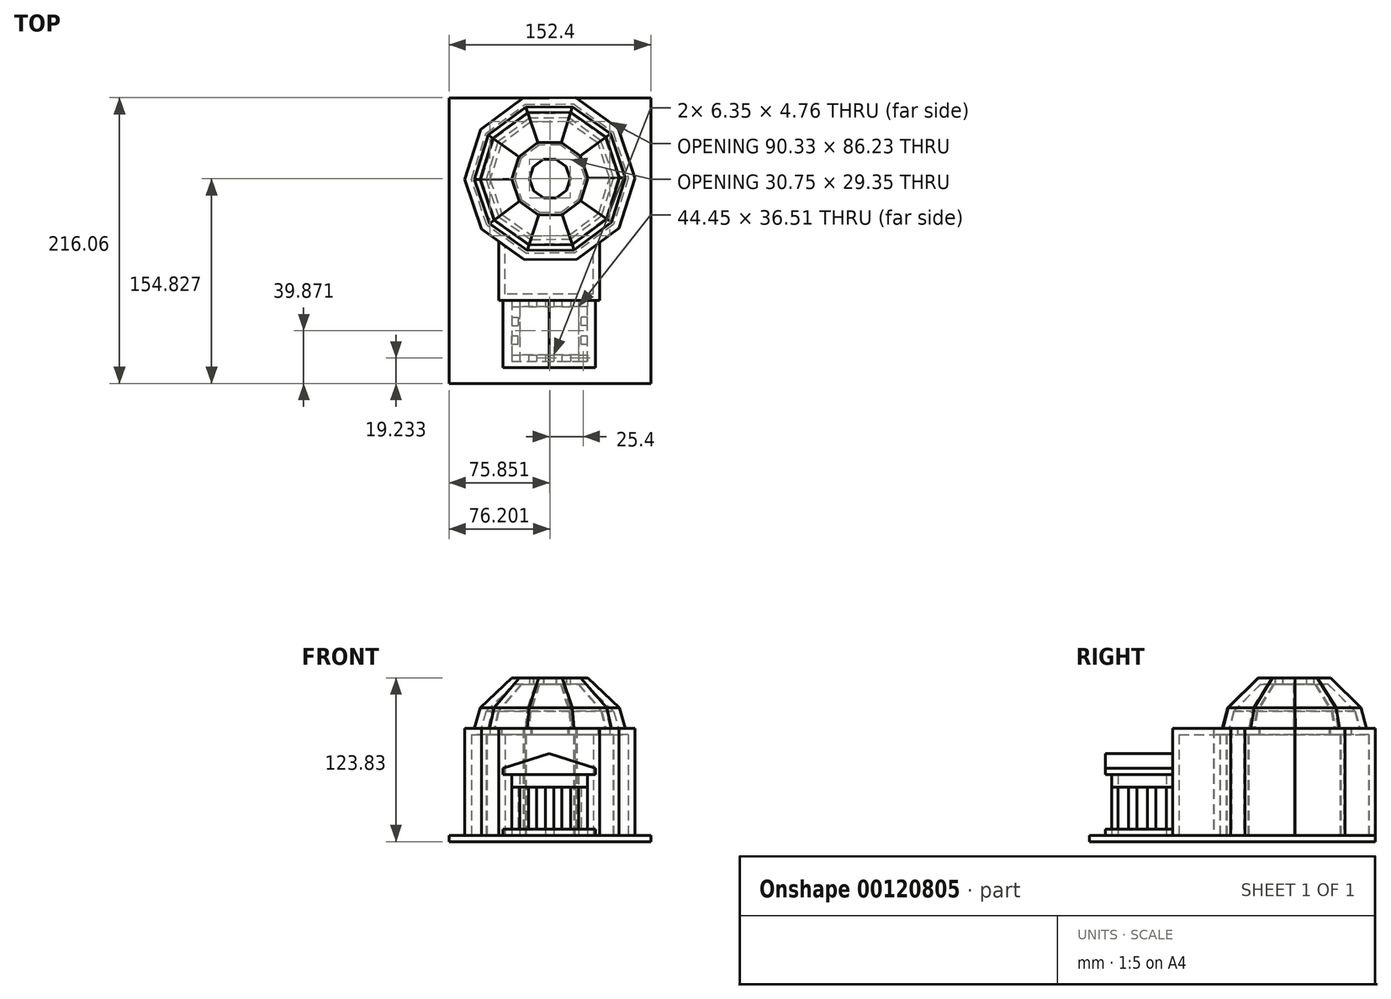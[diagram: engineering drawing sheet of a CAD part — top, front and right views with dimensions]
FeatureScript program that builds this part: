
annotation { "Feature Type Name" : "Feature", "Feature Type Description" : "" }
export const myFeature = defineFeature(function(context is Context, id is Id, definition is map)
    precondition{}
    {
        {
            var Q0;
            Q0=qCreatedBy(makeId("Top.planeOp"),FACE);
            var sketch = newSketch(context, id + "F0", { "sketchPlane" : qUnion([Q0])});
            skLineSegment(sketch, "E0.bottom", {"start": v(-75.7, 133.56) * mm, "end": v(76.7, 133.56) * mm});
            skLineSegment(sketch, "E0.top", {"start": v(-75.7, -82.34) * mm, "end": v(76.7, -82.34) * mm});
            skLineSegment(sketch, "E0.left", {"start": v(-75.7, 133.56) * mm, "end": v(-75.7, -82.34) * mm});
            skLineSegment(sketch, "E0.right", {"start": v(76.7, 133.56) * mm, "end": v(76.7, -82.34) * mm});
            skSolve(sketch);
        }
        {
            var Q0;
            Q0=qSketchRegion(id+"F0",true);
            var Q1;
            Q1=qSketchRegion(id+"FxzeoTgwMsGnq95_1",true);
            extrude(context, id + "F1", {"entities" : qUnion([Q0, Q1]), "depth" : 4.76 * mm});
        }
        {
            var Q0;
            Q0=makeQuery(id+"F1.opExtrude","CAP_FACE",FACE,{"disambiguationData":[OSD([sQuery(id+"F0.wireOp",EDGE,"E0.bottom"),sQuery(id+"F0.wireOp",EDGE,"E0.top"),sQuery(id+"F0.wireOp",EDGE,"E0.left"),sQuery(id+"F0.wireOp",EDGE,"E0.right")])],"isStart":false});
            var sketch = newSketch(context, id + "F2", { "sketchPlane" : qUnion([Q0])});
            skCircle(sketch, "E1.cCircle", {"center": v(0.5, 72.49) * mm, "radius": 61.07 * mm, "construction": true});
            skPoint(sketch, "E1.cCircle.centerSnap0", {"position": v(0.5, 133.56) * mm});
            skPoint(sketch, "E1.cCircle.perimeterSnap0", {"position": v(0.5, 133.56) * mm});
            skLineSegment(sketch, "E1.0", {"start": v(-19.84, 133.4) * mm, "end": v(19.84, 133.72) * mm});
            skLineSegment(sketch, "E1.1", {"start": v(19.84, 133.72) * mm, "end": v(52.14, 110.65) * mm});
            skLineSegment(sketch, "E1.2", {"start": v(52.14, 110.65) * mm, "end": v(64.7, 73) * mm});
            skLineSegment(sketch, "E1.3", {"start": v(64.7, 73) * mm, "end": v(52.74, 35.16) * mm});
            skLineSegment(sketch, "E1.4", {"start": v(52.74, 35.16) * mm, "end": v(20.82, 11.58) * mm});
            skLineSegment(sketch, "E1.5", {"start": v(20.82, 11.58) * mm, "end": v(-18.86, 11.26) * mm});
            skLineSegment(sketch, "E1.6", {"start": v(-18.86, 11.26) * mm, "end": v(-51.16, 34.33) * mm});
            skLineSegment(sketch, "E1.7", {"start": v(-51.16, 34.33) * mm, "end": v(-63.72, 71.97) * mm});
            skLineSegment(sketch, "E1.8", {"start": v(-63.72, 71.97) * mm, "end": v(-51.76, 109.81) * mm});
            skLineSegment(sketch, "E1.9", {"start": v(-51.76, 109.81) * mm, "end": v(-19.84, 133.4) * mm});
            skPoint(sketch, "E1.0.midPoint", {"position": v(0, 133.56) * mm});
            skPoint(sketch, "E1.0.midPoint.positionSnap0", {"position": v(0.5, 133.56) * mm});
            skCircle(sketch, "E2.cCircle", {"center": v(0.5, 72.49) * mm, "radius": 42.96 * mm, "construction": true});
            skLineSegment(sketch, "E2.0", {"start": v(-13.96, 115.28) * mm, "end": v(13.96, 115.6) * mm});
            skLineSegment(sketch, "E2.1", {"start": v(13.96, 115.6) * mm, "end": v(36.73, 99.45) * mm});
            skLineSegment(sketch, "E2.2", {"start": v(36.73, 99.45) * mm, "end": v(45.65, 73) * mm});
            skLineSegment(sketch, "E2.3", {"start": v(45.65, 73) * mm, "end": v(37.33, 46.36) * mm});
            skLineSegment(sketch, "E2.4", {"start": v(37.33, 46.36) * mm, "end": v(14.94, 29.7) * mm});
            skLineSegment(sketch, "E2.5", {"start": v(14.94, 29.7) * mm, "end": v(-12.97, 29.37) * mm});
            skLineSegment(sketch, "E2.6", {"start": v(-12.97, 29.37) * mm, "end": v(-35.74, 45.52) * mm});
            skLineSegment(sketch, "E2.7", {"start": v(-35.74, 45.52) * mm, "end": v(-44.67, 71.97) * mm});
            skLineSegment(sketch, "E2.8", {"start": v(-44.67, 71.97) * mm, "end": v(-36.35, 98.62) * mm});
            skLineSegment(sketch, "E2.9", {"start": v(-36.35, 98.62) * mm, "end": v(-13.96, 115.28) * mm});
            skPoint(sketch, "E2.0.midPoint", {"position": v(0, 115.44) * mm});
            skSolve(sketch);
        }
        {
            var Q0;
            Q0=qSketchRegion(id+"F2",true);
            var Q1;
            Q1=makeQuery(id+"F2.imprint","IMPRINT",FACE,{"disambiguationData":[TD([[makeQuery(id+"F2.imprint","IMPRINT",EDGE,{"derivedFrom":sQuery(id+"F2.wireOp",EDGE,"E2.0")}),-1.0]])]});
            extrude(context, id + "F3", {"entities" : qUnion([Q0, Q1]), "depth" : 80.96 * mm});
        }
        {
            var Q0;
            Q0=makeQuery(id+"F3.opExtrude","CAP_FACE",FACE,{"disambiguationData":[OSD([sQuery(id+"F2.wireOp",EDGE,"E1.0"),sQuery(id+"F2.wireOp",EDGE,"E1.1"),sQuery(id+"F2.wireOp",EDGE,"E1.2"),sQuery(id+"F2.wireOp",EDGE,"E1.3"),sQuery(id+"F2.wireOp",EDGE,"E1.4"),sQuery(id+"F2.wireOp",EDGE,"E1.5"),sQuery(id+"F2.wireOp",EDGE,"E1.6"),sQuery(id+"F2.wireOp",EDGE,"E1.7"),sQuery(id+"F2.wireOp",EDGE,"E1.8"),sQuery(id+"F2.wireOp",EDGE,"E1.9")])],"isStart":true});
            shell(context, id + "F4", {"entities" : qUnion([Q0]), "thickness" : 4.76 * mm});
        }
        {
            var Q0;
            Q0=makeQuery(id+"F2.imprint","IMPRINT",FACE,{"disambiguationData":[TD([[makeQuery(id+"F2.imprint","IMPRINT",EDGE,{"derivedFrom":sQuery(id+"F2.wireOp",EDGE,"E2.0")}),-1.0]])]});
            extrude(context, id + "F5", {"entities" : qUnion([Q0]), "operationType" : NewBodyOperationType.REMOVE, "endBound" : BoundingType.THROUGH_ALL, "depth" : 148.13 * mm});
        }
        {
            var Q0;
            Q0=makeQuery(id+"F1.opExtrude","CAP_FACE",FACE,{"disambiguationData":[OSD([sQuery(id+"F0.wireOp",EDGE,"E0.bottom"),sQuery(id+"F0.wireOp",EDGE,"E0.top"),sQuery(id+"F0.wireOp",EDGE,"E0.left"),sQuery(id+"F0.wireOp",EDGE,"E0.right")])],"isStart":false});
            var sketch = newSketch(context, id + "F6", { "sketchPlane" : qUnion([Q0])});
            skLineSegment(sketch, "E3.bottom", {"start": v(38.1, -19.45) * mm, "end": v(-38.1, -19.45) * mm});
            skLineSegment(sketch, "E3.top", {"start": v(38.1, 25) * mm, "end": v(-38.1, 25) * mm});
            skLineSegment(sketch, "E3.left", {"start": v(38.1, -19.45) * mm, "end": v(38.1, 25) * mm});
            skLineSegment(sketch, "E3.right", {"start": v(-38.1, -19.45) * mm, "end": v(-38.1, 25) * mm});
            skPoint(sketch, "E3.middle", {"position": v(0, 2.77) * mm});
            skLineSegment(sketch, "E4.0", {"start": v(-18.86, 11.26) * mm, "end": v(-51.16, 34.33) * mm});
            skLineSegment(sketch, "E5.0", {"start": v(20.82, 11.58) * mm, "end": v(-18.86, 11.26) * mm});
            skLineSegment(sketch, "E6.0", {"start": v(52.74, 35.16) * mm, "end": v(20.82, 11.58) * mm});
            skSolve(sketch);
        }
        {
            var Q0;
            {var subQ4=sQuery(id+"F6.wireOp",EDGE,"E3.bottom");Q0=makeQuery(id+"F6.imprint","IMPRINT",FACE,{"disambiguationData":[TD([[makeQuery(id+"F6.imprint","IMPRINT",EDGE,{"derivedFrom":subQ4}),-1.0]])]});}
            extrude(context, id + "F7", {"entities" : qUnion([Q0]), "depth" : 80.96 * mm});
        }
        {
            var Q0;
            Q0=makeQuery(id+"F7.opExtrude","CAP_FACE",FACE,{"disambiguationData":[OSD([sQuery(id+"F6.wireOp",EDGE,"E3.bottom"),sQuery(id+"F6.wireOp",EDGE,"E3.left"),sQuery(id+"F6.wireOp",EDGE,"E3.right"),sQuery(id+"F6.wireOp",EDGE,"E4.0"),sQuery(id+"F6.wireOp",EDGE,"E5.0"),sQuery(id+"F6.wireOp",EDGE,"E6.0")])],"isStart":true});
            var Q1;
            Q1=makeQuery(id+"F7.opExtrude","SWEPT_FACE",FACE,{"disambiguationData":[OSD([sQuery(id+"F6.wireOp",EDGE,"E5.0")])]});
            var Q2;
            Q2=makeQuery(id+"F7.opExtrude","SWEPT_FACE",FACE,{"disambiguationData":[OSD([sQuery(id+"F6.wireOp",EDGE,"E4.0")])]});
            var Q3;
            Q3=makeQuery(id+"F7.opExtrude","SWEPT_FACE",FACE,{"disambiguationData":[OSD([sQuery(id+"F6.wireOp",EDGE,"E6.0")])]});
            shell(context, id + "F8", {"entities" : qUnion([Q0, Q1, Q2, Q3]), "thickness" : 4.76 * mm});
        }
        {
            var Q0;
            Q0=makeQuery(id+"F1.opExtrude","CAP_FACE",FACE,{"disambiguationData":[OSD([sQuery(id+"F0.wireOp",EDGE,"E0.bottom"),sQuery(id+"F0.wireOp",EDGE,"E0.top"),sQuery(id+"F0.wireOp",EDGE,"E0.left"),sQuery(id+"F0.wireOp",EDGE,"E0.right")])],"isStart":false});
            var sketch = newSketch(context, id + "F9", { "sketchPlane" : qUnion([Q0])});
            skLineSegment(sketch, "E7.bottom", {"start": v(34.92, -70.25) * mm, "end": v(-34.93, -70.25) * mm});
            skLineSegment(sketch, "E7.top", {"start": v(34.93, -19.45) * mm, "end": v(-34.93, -19.45) * mm});
            skLineSegment(sketch, "E7.left", {"start": v(34.93, -70.25) * mm, "end": v(34.93, -19.45) * mm});
            skLineSegment(sketch, "E7.right", {"start": v(-34.93, -70.25) * mm, "end": v(-34.93, -19.45) * mm});
            skPoint(sketch, "E7.middle", {"position": v(0, -44.85) * mm});
            skLineSegment(sketch, "E8.bottom", {"start": v(-28.43, -60.73) * mm, "end": v(-22.08, -60.73) * mm});
            skLineSegment(sketch, "E8.top", {"start": v(-28.43, -65.49) * mm, "end": v(-22.08, -65.49) * mm});
            skLineSegment(sketch, "E8.left", {"start": v(-28.43, -60.73) * mm, "end": v(-28.43, -65.49) * mm});
            skLineSegment(sketch, "E8.right", {"start": v(-22.08, -60.73) * mm, "end": v(-22.08, -65.49) * mm});
            skLineSegment(sketch, "E9.1.0.0", {"start": v(-9.38, -60.73) * mm, "end": v(-9.38, -65.49) * mm});
            skLineSegment(sketch, "E9.1.0.1", {"start": v(-15.73, -60.73) * mm, "end": v(-15.73, -65.49) * mm});
            skLineSegment(sketch, "E9.1.0.2", {"start": v(-15.73, -65.49) * mm, "end": v(-9.38, -65.49) * mm});
            skLineSegment(sketch, "E9.1.0.3", {"start": v(-15.73, -60.73) * mm, "end": v(-9.38, -60.73) * mm});
            skLineSegment(sketch, "E9.2.0.0", {"start": v(3.32, -60.73) * mm, "end": v(3.32, -65.49) * mm});
            skLineSegment(sketch, "E9.2.0.1", {"start": v(-3.03, -60.73) * mm, "end": v(-3.03, -65.49) * mm});
            skLineSegment(sketch, "E9.2.0.2", {"start": v(-3.03, -65.49) * mm, "end": v(3.32, -65.49) * mm});
            skLineSegment(sketch, "E9.2.0.3", {"start": v(-3.03, -60.73) * mm, "end": v(3.32, -60.73) * mm});
            skLineSegment(sketch, "E9.3.0.0", {"start": v(16.02, -60.73) * mm, "end": v(16.02, -65.49) * mm});
            skLineSegment(sketch, "E9.3.0.1", {"start": v(9.67, -60.73) * mm, "end": v(9.67, -65.49) * mm});
            skLineSegment(sketch, "E9.3.0.2", {"start": v(9.67, -65.49) * mm, "end": v(16.02, -65.49) * mm});
            skLineSegment(sketch, "E9.3.0.3", {"start": v(9.67, -60.73) * mm, "end": v(16.02, -60.73) * mm});
            skLineSegment(sketch, "E9.4.0.0", {"start": v(28.72, -60.73) * mm, "end": v(28.72, -65.49) * mm});
            skLineSegment(sketch, "E9.4.0.1", {"start": v(22.37, -60.73) * mm, "end": v(22.37, -65.49) * mm});
            skLineSegment(sketch, "E9.4.0.2", {"start": v(22.37, -65.49) * mm, "end": v(28.72, -65.49) * mm});
            skLineSegment(sketch, "E9.4.0.3", {"start": v(22.37, -60.73) * mm, "end": v(28.72, -60.73) * mm});
            skLineSegment(sketch, "E9.direction1", {"start": v(-28.43, -65.49) * mm, "end": v(-15.73, -65.49) * mm, "construction": true});
            skLineSegment(sketch, "E10.1.0.3", {"start": v(-3.03, -65.49) * mm, "end": v(9.67, -65.49) * mm, "construction": true});
            skLineSegment(sketch, "E10.2.0.3", {"start": v(22.37, -65.49) * mm, "end": v(35.07, -65.49) * mm, "construction": true});
            skLineSegment(sketch, "E10.direction1", {"start": v(-28.43, -65.49) * mm, "end": v(-3.03, -65.49) * mm, "construction": true});
            skLineSegment(sketch, "E11.0.1.0", {"start": v(28.72, -38.5) * mm, "end": v(23.95, -38.5) * mm});
            skLineSegment(sketch, "E11.0.1.1", {"start": v(28.72, -38.5) * mm, "end": v(28.72, -32.15) * mm});
            skLineSegment(sketch, "E11.0.1.2", {"start": v(23.95, -38.5) * mm, "end": v(23.95, -32.15) * mm});
            skLineSegment(sketch, "E11.0.1.3", {"start": v(28.72, -32.15) * mm, "end": v(23.95, -32.15) * mm});
            skLineSegment(sketch, "E12.bottom", {"start": v(28.72, -19.45) * mm, "end": v(22.37, -19.45) * mm});
            skLineSegment(sketch, "E12.top", {"start": v(28.72, -24.21) * mm, "end": v(22.37, -24.21) * mm});
            skLineSegment(sketch, "E12.left", {"start": v(28.72, -19.45) * mm, "end": v(28.72, -24.21) * mm});
            skLineSegment(sketch, "E12.right", {"start": v(22.37, -19.45) * mm, "end": v(22.37, -24.21) * mm});
            skLineSegment(sketch, "E13.bottom", {"start": v(28.72, -52.79) * mm, "end": v(23.95, -52.79) * mm});
            skLineSegment(sketch, "E13.top", {"start": v(28.72, -46.44) * mm, "end": v(23.95, -46.44) * mm});
            skLineSegment(sketch, "E13.left", {"start": v(28.72, -52.79) * mm, "end": v(28.72, -46.44) * mm});
            skLineSegment(sketch, "E13.right", {"start": v(23.95, -52.79) * mm, "end": v(23.95, -46.44) * mm});
            skLineSegment(sketch, "E14.bottom", {"start": v(-28.43, -19.45) * mm, "end": v(-22.08, -19.45) * mm});
            skLineSegment(sketch, "E14.top", {"start": v(-28.43, -24.23) * mm, "end": v(-22.08, -24.23) * mm});
            skLineSegment(sketch, "E14.left", {"start": v(-28.43, -19.45) * mm, "end": v(-28.43, -24.23) * mm});
            skLineSegment(sketch, "E14.right", {"start": v(-22.08, -19.45) * mm, "end": v(-22.08, -24.23) * mm});
            skLineSegment(sketch, "E15.bottom", {"start": v(-28.43, -32.15) * mm, "end": v(-23.67, -32.15) * mm});
            skLineSegment(sketch, "E15.top", {"start": v(-28.43, -38.5) * mm, "end": v(-23.67, -38.5) * mm});
            skLineSegment(sketch, "E15.left", {"start": v(-28.43, -32.15) * mm, "end": v(-28.43, -38.5) * mm});
            skLineSegment(sketch, "E15.right", {"start": v(-23.67, -32.15) * mm, "end": v(-23.67, -38.5) * mm});
            skLineSegment(sketch, "E16.bottom", {"start": v(-23.67, -52.79) * mm, "end": v(-28.43, -52.79) * mm});
            skLineSegment(sketch, "E16.top", {"start": v(-23.67, -46.44) * mm, "end": v(-28.43, -46.44) * mm});
            skLineSegment(sketch, "E16.left", {"start": v(-23.67, -52.79) * mm, "end": v(-23.67, -46.44) * mm});
            skLineSegment(sketch, "E16.right", {"start": v(-28.43, -52.79) * mm, "end": v(-28.43, -46.44) * mm});
            skLineSegment(sketch, "E17.1.0.0", {"start": v(-15.73, -24.23) * mm, "end": v(-9.38, -24.23) * mm});
            skLineSegment(sketch, "E17.1.0.1", {"start": v(-9.38, -19.45) * mm, "end": v(-9.38, -24.23) * mm});
            skLineSegment(sketch, "E17.1.0.2", {"start": v(-15.73, -19.45) * mm, "end": v(-15.73, -24.23) * mm});
            skLineSegment(sketch, "E17.2.0.0", {"start": v(-3.03, -24.23) * mm, "end": v(3.32, -24.23) * mm});
            skLineSegment(sketch, "E17.2.0.1", {"start": v(3.32, -19.45) * mm, "end": v(3.32, -24.23) * mm});
            skLineSegment(sketch, "E17.2.0.2", {"start": v(-3.03, -19.45) * mm, "end": v(-3.03, -24.23) * mm});
            skLineSegment(sketch, "E17.3.0.0", {"start": v(9.67, -24.23) * mm, "end": v(16.02, -24.23) * mm});
            skLineSegment(sketch, "E17.3.0.1", {"start": v(16.02, -19.45) * mm, "end": v(16.02, -24.23) * mm});
            skLineSegment(sketch, "E17.3.0.2", {"start": v(9.67, -19.45) * mm, "end": v(9.67, -24.23) * mm});
            skLineSegment(sketch, "E17.direction1", {"start": v(-28.43, -24.23) * mm, "end": v(-15.73, -24.23) * mm, "construction": true});
            skSolve(sketch);
        }
        {
            var Q0;
            Q0=makeQuery(id+"F9.imprint","IMPRINT",FACE,{"disambiguationData":[TD([[makeQuery(id+"F9.imprint","IMPRINT",EDGE,{"derivedFrom":sQuery(id+"F9.wireOp",EDGE,"E17.3.0.0")}),1.0]])]});
            var Q1;
            Q1=makeQuery(id+"F9.imprint","IMPRINT",FACE,{"disambiguationData":[TD([[makeQuery(id+"F9.imprint","IMPRINT",EDGE,{"derivedFrom":sQuery(id+"F9.wireOp",EDGE,"E17.2.0.0")}),1.0]])]});
            var Q2;
            Q2=makeQuery(id+"F9.imprint","IMPRINT",FACE,{"disambiguationData":[TD([[makeQuery(id+"F9.imprint","IMPRINT",EDGE,{"derivedFrom":sQuery(id+"F9.wireOp",EDGE,"E17.1.0.0")}),1.0]])]});
            var Q3;
            Q3=makeQuery(id+"F9.imprint","IMPRINT",FACE,{"disambiguationData":[TD([[makeQuery(id+"F9.imprint","IMPRINT",EDGE,{"derivedFrom":sQuery(id+"F9.wireOp",EDGE,"E12.bottom")}),1.0]])]});
            var Q4;
            Q4=makeQuery(id+"F9.imprint","IMPRINT",FACE,{"disambiguationData":[TD([[makeQuery(id+"F9.imprint","IMPRINT",EDGE,{"derivedFrom":sQuery(id+"F9.wireOp",EDGE,"E14.bottom")}),-1.0]])]});
            var Q5;
            Q5=makeQuery(id+"F9.imprint","IMPRINT",FACE,{"disambiguationData":[TD([[makeQuery(id+"F9.imprint","IMPRINT",EDGE,{"derivedFrom":sQuery(id+"F9.wireOp",EDGE,"E16.bottom")}),-1.0]])]});
            var Q6;
            Q6=makeQuery(id+"F9.imprint","IMPRINT",FACE,{"disambiguationData":[TD([[makeQuery(id+"F9.imprint","IMPRINT",EDGE,{"derivedFrom":sQuery(id+"F9.wireOp",EDGE,"E8.bottom")}),-1.0]])]});
            var Q7;
            Q7=makeQuery(id+"F9.imprint","IMPRINT",FACE,{"disambiguationData":[TD([[makeQuery(id+"F9.imprint","IMPRINT",EDGE,{"derivedFrom":sQuery(id+"F9.wireOp",EDGE,"E15.bottom")}),-1.0]])]});
            var Q8;
            Q8=makeQuery(id+"F9.imprint","IMPRINT",FACE,{"disambiguationData":[TD([[makeQuery(id+"F9.imprint","IMPRINT",EDGE,{"derivedFrom":sQuery(id+"F9.wireOp",EDGE,"E9.1.0.0")}),-1.0]])]});
            var Q9;
            Q9=makeQuery(id+"F9.imprint","IMPRINT",FACE,{"disambiguationData":[TD([[makeQuery(id+"F9.imprint","IMPRINT",EDGE,{"derivedFrom":sQuery(id+"F9.wireOp",EDGE,"E7.bottom")}),-1.0]])]});
            var Q10;
            Q10=makeQuery(id+"F9.imprint","IMPRINT",FACE,{"disambiguationData":[TD([[makeQuery(id+"F9.imprint","IMPRINT",EDGE,{"derivedFrom":sQuery(id+"F9.wireOp",EDGE,"E11.0.1.0")}),-1.0]])]});
            var Q11;
            Q11=makeQuery(id+"F9.imprint","IMPRINT",FACE,{"disambiguationData":[TD([[makeQuery(id+"F9.imprint","IMPRINT",EDGE,{"derivedFrom":sQuery(id+"F9.wireOp",EDGE,"E13.bottom")}),-1.0]])]});
            var Q12;
            Q12=makeQuery(id+"F9.imprint","IMPRINT",FACE,{"disambiguationData":[TD([[makeQuery(id+"F9.imprint","IMPRINT",EDGE,{"derivedFrom":sQuery(id+"F9.wireOp",EDGE,"E9.4.0.1")}),1.0]])]});
            var Q13;
            Q13=makeQuery(id+"F9.imprint","IMPRINT",FACE,{"disambiguationData":[TD([[makeQuery(id+"F9.imprint","IMPRINT",EDGE,{"derivedFrom":sQuery(id+"F9.wireOp",EDGE,"E9.3.0.0")}),-1.0]])]});
            var Q14;
            Q14=makeQuery(id+"F9.imprint","IMPRINT",FACE,{"disambiguationData":[TD([[makeQuery(id+"F9.imprint","IMPRINT",EDGE,{"derivedFrom":sQuery(id+"F9.wireOp",EDGE,"E9.2.0.1")}),1.0]])]});
            extrude(context, id + "F10", {"entities" : qUnion([Q0, Q1, Q2, Q3, Q4, Q5, Q6, Q7, Q8, Q9, Q10, Q11, Q12, Q13, Q14]), "depth" : 4.76 * mm});
        }
        {
            var Q0;
            Q0=makeQuery(id+"F10.opExtrude","CAP_FACE",FACE,{"disambiguationData":[OSD([sQuery(id+"F9.wireOp",EDGE,"E7.bottom"),sQuery(id+"F9.wireOp",EDGE,"E7.top"),sQuery(id+"F9.wireOp",EDGE,"E7.left"),sQuery(id+"F9.wireOp",EDGE,"E7.right"),sQuery(id+"F9.wireOp",EDGE,"E12.bottom"),sQuery(id+"F9.wireOp",EDGE,"E14.bottom")])],"isStart":false});
            var sketch = newSketch(context, id + "F11", { "sketchPlane" : qUnion([Q0])});
            skLineSegment(sketch, "E18.0", {"start": v(-28.43, -24.23) * mm, "end": v(-22.08, -24.23) * mm});
            skLineSegment(sketch, "E19.0", {"start": v(-22.08, -19.45) * mm, "end": v(-22.08, -24.23) * mm});
            skLineSegment(sketch, "E20.0", {"start": v(34.93, -19.45) * mm, "end": v(-34.93, -19.45) * mm});
            skLineSegment(sketch, "E21.0", {"start": v(-28.43, -19.45) * mm, "end": v(-28.43, -24.23) * mm});
            skLineSegment(sketch, "E22.0", {"start": v(-15.73, -19.45) * mm, "end": v(-15.73, -24.23) * mm});
            skLineSegment(sketch, "E23.0", {"start": v(-15.73, -24.23) * mm, "end": v(-9.38, -24.23) * mm});
            skLineSegment(sketch, "E24.0", {"start": v(-9.38, -19.45) * mm, "end": v(-9.38, -24.23) * mm});
            skLineSegment(sketch, "E25.0", {"start": v(-3.03, -19.45) * mm, "end": v(-3.03, -24.23) * mm});
            skLineSegment(sketch, "E26.0", {"start": v(-3.03, -24.23) * mm, "end": v(3.32, -24.23) * mm});
            skLineSegment(sketch, "E27.0", {"start": v(3.32, -19.45) * mm, "end": v(3.32, -24.23) * mm});
            skLineSegment(sketch, "E28.0", {"start": v(-23.67, -32.15) * mm, "end": v(-23.67, -38.5) * mm});
            skLineSegment(sketch, "E29.0", {"start": v(-28.43, -32.15) * mm, "end": v(-23.67, -32.15) * mm});
            skLineSegment(sketch, "E30.0", {"start": v(-28.43, -32.15) * mm, "end": v(-28.43, -38.5) * mm});
            skLineSegment(sketch, "E31.0", {"start": v(-28.43, -38.5) * mm, "end": v(-23.67, -38.5) * mm});
            skLineSegment(sketch, "E32.0", {"start": v(-23.67, -46.44) * mm, "end": v(-28.43, -46.44) * mm});
            skLineSegment(sketch, "E33.0", {"start": v(-28.43, -52.79) * mm, "end": v(-28.43, -46.44) * mm});
            skLineSegment(sketch, "E34.0", {"start": v(-23.67, -52.79) * mm, "end": v(-28.43, -52.79) * mm});
            skLineSegment(sketch, "E35.0", {"start": v(-23.67, -52.79) * mm, "end": v(-23.67, -46.44) * mm});
            skLineSegment(sketch, "E36.0", {"start": v(-28.43, -60.73) * mm, "end": v(-22.08, -60.73) * mm});
            skLineSegment(sketch, "E37.0", {"start": v(-28.43, -60.73) * mm, "end": v(-28.43, -65.49) * mm});
            skLineSegment(sketch, "E38.0", {"start": v(-28.43, -65.49) * mm, "end": v(-22.08, -65.49) * mm});
            skLineSegment(sketch, "E39.0", {"start": v(-22.08, -60.73) * mm, "end": v(-22.08, -65.49) * mm});
            skLineSegment(sketch, "E40.0", {"start": v(-15.73, -60.73) * mm, "end": v(-15.73, -65.49) * mm});
            skLineSegment(sketch, "E41.0", {"start": v(-15.73, -60.73) * mm, "end": v(-9.38, -60.73) * mm});
            skLineSegment(sketch, "E42.0", {"start": v(-9.38, -60.73) * mm, "end": v(-9.38, -65.49) * mm});
            skLineSegment(sketch, "E43.0", {"start": v(-15.73, -65.49) * mm, "end": v(-9.38, -65.49) * mm});
            skLineSegment(sketch, "E44.0", {"start": v(-3.03, -60.73) * mm, "end": v(-3.03, -65.49) * mm});
            skLineSegment(sketch, "E45.0", {"start": v(-3.03, -60.73) * mm, "end": v(3.32, -60.73) * mm});
            skLineSegment(sketch, "E46.0", {"start": v(3.32, -60.73) * mm, "end": v(3.32, -65.49) * mm});
            skLineSegment(sketch, "E47.0", {"start": v(-3.03, -65.49) * mm, "end": v(3.32, -65.49) * mm});
            skLineSegment(sketch, "E48.0", {"start": v(9.67, -60.73) * mm, "end": v(9.67, -65.49) * mm});
            skLineSegment(sketch, "E49.0", {"start": v(9.67, -60.73) * mm, "end": v(16.02, -60.73) * mm});
            skLineSegment(sketch, "E50.0", {"start": v(16.02, -60.73) * mm, "end": v(16.02, -65.49) * mm});
            skLineSegment(sketch, "E50.1", {"start": v(9.67, -65.49) * mm, "end": v(16.02, -65.49) * mm});
            skLineSegment(sketch, "E51.0", {"start": v(22.37, -60.73) * mm, "end": v(22.37, -65.49) * mm});
            skLineSegment(sketch, "E51.1", {"start": v(22.37, -60.73) * mm, "end": v(28.72, -60.73) * mm});
            skLineSegment(sketch, "E52.1", {"start": v(28.72, -60.73) * mm, "end": v(28.72, -65.49) * mm});
            skLineSegment(sketch, "E52.2", {"start": v(22.37, -65.49) * mm, "end": v(28.72, -65.49) * mm});
            skLineSegment(sketch, "E53.0", {"start": v(23.95, -52.79) * mm, "end": v(23.95, -46.44) * mm});
            skLineSegment(sketch, "E53.1", {"start": v(28.72, -46.44) * mm, "end": v(23.95, -46.44) * mm});
            skLineSegment(sketch, "E53.2", {"start": v(28.72, -52.79) * mm, "end": v(28.72, -46.44) * mm});
            skLineSegment(sketch, "E53.3", {"start": v(28.72, -52.79) * mm, "end": v(23.95, -52.79) * mm});
            skLineSegment(sketch, "E53.4", {"start": v(28.72, -38.5) * mm, "end": v(23.95, -38.5) * mm});
            skLineSegment(sketch, "E53.5", {"start": v(23.95, -38.5) * mm, "end": v(23.95, -32.15) * mm});
            skLineSegment(sketch, "E53.6", {"start": v(28.72, -32.15) * mm, "end": v(23.95, -32.15) * mm});
            skLineSegment(sketch, "E53.7", {"start": v(28.72, -38.5) * mm, "end": v(28.72, -32.15) * mm});
            skLineSegment(sketch, "E53.8", {"start": v(28.72, -24.21) * mm, "end": v(22.37, -24.21) * mm});
            skLineSegment(sketch, "E53.9", {"start": v(22.37, -19.45) * mm, "end": v(22.37, -24.21) * mm});
            skLineSegment(sketch, "E53.10", {"start": v(28.72, -19.45) * mm, "end": v(28.72, -24.21) * mm});
            skLineSegment(sketch, "E53.11", {"start": v(16.02, -19.45) * mm, "end": v(16.02, -24.23) * mm});
            skLineSegment(sketch, "E53.12", {"start": v(9.67, -19.45) * mm, "end": v(9.67, -24.23) * mm});
            skLineSegment(sketch, "E53.13", {"start": v(9.67, -24.23) * mm, "end": v(16.02, -24.23) * mm});
            skSolve(sketch);
        }
        {
            var Q0;
            Q0=qSketchRegion(id+"F11",true);
            extrude(context, id + "F12", {"entities" : qUnion([Q0]), "depth" : 31.75 * mm});
        }
        {
            var Q0;
            Q0=makeQuery(id+"F9.imprint","IMPRINT",FACE,{"disambiguationData":[TD([[makeQuery(id+"F9.imprint","IMPRINT",EDGE,{"derivedFrom":sQuery(id+"F9.wireOp",EDGE,"E7.bottom")}),1.0]])]});
            var sketch = newSketch(context, id + "F13", { "sketchPlane" : qUnion([Q0])});
            skLineSegment(sketch, "E54.0", {"start": v(-34.93, -70.25) * mm, "end": v(-34.93, -19.45) * mm});
            skLineSegment(sketch, "E55.0", {"start": v(34.93, -70.25) * mm, "end": v(34.93, -19.45) * mm});
            skLineSegment(sketch, "E56.0", {"start": v(34.93, -70.25) * mm, "end": v(-34.93, -70.25) * mm});
            skLineSegment(sketch, "E57.top", {"start": v(34.93, -19.45) * mm, "end": v(-34.93, -19.45) * mm});
            skSolve(sketch);
        }
        {
            var Q0;
            Q0=makeQuery(id+"F13.imprint","IMPRINT",FACE,{"disambiguationData":[TD([[makeQuery(id+"F13.imprint","IMPRINT",EDGE,{"derivedFrom":sQuery(id+"F13.wireOp",EDGE,"E56.0")}),1.0]])]});
            var sketch = newSketch(context, id + "F14", { "sketchPlane" : qUnion([Q0])});
            skLineSegment(sketch, "E58.0", {"start": v(-34.93, -70.25) * mm, "end": v(-34.93, -19.45) * mm});
            skLineSegment(sketch, "E59.0", {"start": v(34.92, -70.25) * mm, "end": v(-34.93, -70.25) * mm});
            skLineSegment(sketch, "E60.0", {"start": v(34.93, -70.25) * mm, "end": v(34.93, -19.45) * mm});
            skLineSegment(sketch, "E61.0", {"start": v(34.93, -19.45) * mm, "end": v(-34.93, -19.45) * mm});
            skSolve(sketch);
        }
        {
            var Q0;
            Q0=makeQuery(id+"F12.opExtrude","CAP_FACE",FACE,{"disambiguationData":[OSD([sQuery(id+"F11.wireOp",EDGE,"E36.0"),sQuery(id+"F11.wireOp",EDGE,"E37.0"),sQuery(id+"F11.wireOp",EDGE,"E38.0"),sQuery(id+"F11.wireOp",EDGE,"E39.0")])],"isStart":false});
            var sketch = newSketch(context, id + "F15", { "sketchPlane" : qUnion([Q0])});
            skPoint(sketch, "E62.0", {"position": v(-28.43, -65.49) * mm});
            skPoint(sketch, "E63.0", {"position": v(28.72, -65.49) * mm});
            skPoint(sketch, "E64.0", {"position": v(28.72, -19.45) * mm});
            skPoint(sketch, "E65.0", {"position": v(-28.43, -19.45) * mm});
            skLineSegment(sketch, "E66.bottom", {"start": v(-28.43, -65.49) * mm, "end": v(28.72, -65.49) * mm});
            skLineSegment(sketch, "E66.top", {"start": v(-28.43, -19.45) * mm, "end": v(28.72, -19.45) * mm});
            skLineSegment(sketch, "E66.left", {"start": v(-28.43, -65.49) * mm, "end": v(-28.43, -19.45) * mm});
            skLineSegment(sketch, "E66.right", {"start": v(28.72, -65.49) * mm, "end": v(28.72, -19.45) * mm});
            skPoint(sketch, "E67.0", {"position": v(-22.08, -24.23) * mm});
            skPoint(sketch, "E68.0", {"position": v(-22.08, -60.73) * mm});
            skPoint(sketch, "E69.0", {"position": v(22.37, -60.73) * mm});
            skPoint(sketch, "E70.0", {"position": v(22.37, -24.21) * mm});
            skLineSegment(sketch, "E71.bottom", {"start": v(22.37, -24.21) * mm, "end": v(-22.08, -24.21) * mm});
            skLineSegment(sketch, "E71.top", {"start": v(22.37, -60.73) * mm, "end": v(-22.08, -60.73) * mm});
            skLineSegment(sketch, "E71.left", {"start": v(22.37, -24.21) * mm, "end": v(22.37, -60.73) * mm});
            skLineSegment(sketch, "E71.right", {"start": v(-22.08, -24.21) * mm, "end": v(-22.08, -60.73) * mm});
            skSolve(sketch);
        }
        {
            var Q0;
            Q0 = qSketchRegion(id + "F15", true);
            extrude(context, id + "F16", {"entities" : qUnion([Q0]), "depth" : 9.52 * mm});
        }
        {
            var Q0;
            Q0=makeQuery(id+"F7.opExtrude","SWEPT_FACE",FACE,{"disambiguationData":[OSD([sQuery(id+"F6.wireOp",EDGE,"E3.bottom")])]});
            var sketch = newSketch(context, id + "F17", { "sketchPlane" : qUnion([Q0])});
            skPoint(sketch, "E72.0", {"position": v(-34.93, 9.53) * mm});
            skPoint(sketch, "E73.0", {"position": v(34.92, 9.53) * mm});
            skPoint(sketch, "E74.0", {"position": v(-28.43, 50.8) * mm});
            skLineSegment(sketch, "E75.bottom", {"start": v(-34.93, 50.8) * mm, "end": v(34.92, 50.8) * mm});
            skLineSegment(sketch, "E75.top", {"start": v(-34.93, 55.56) * mm, "end": v(34.92, 55.56) * mm});
            skLineSegment(sketch, "E75.left", {"start": v(-34.93, 50.8) * mm, "end": v(-34.93, 55.56) * mm});
            skLineSegment(sketch, "E75.right", {"start": v(34.92, 50.8) * mm, "end": v(34.92, 55.56) * mm});
            skLineSegment(sketch, "E76", {"start": v(-34.93, 55.56) * mm, "end": v(0, 66.68) * mm});
            skLineSegment(sketch, "E77", {"start": v(0, 66.68) * mm, "end": v(34.92, 55.56) * mm});
            skLineSegment(sketch, "E78.0", {"start": v(34.92, 9.53) * mm, "end": v(-34.93, 9.53) * mm});
            skSolve(sketch);
        }
        {
            var Q0;
            Q0 = qSketchRegion(id + "F17", true);
            extrude(context, id + "F18", {"entities" : qUnion([Q0]), "depth" : 50.8 * mm});
        }
        {
            var Q0;
            Q0=qCreatedBy(makeId("Right.planeOp"),FACE);
            var sketch = newSketch(context, id + "F19", { "sketchPlane" : qUnion([Q0])});
            skLineSegment(sketch, "E79.0", {"start": v(11.58, 85.73) * mm, "end": v(11.26, 85.73) * mm});
            skLineSegment(sketch, "E80.0", {"start": v(133.4, 85.73) * mm, "end": v(133.72, 85.73) * mm});
            skLineSegment(sketch, "E81", {"start": v(11.58, 85.73) * mm, "end": v(133.4, 85.73) * mm});
            skLineSegment(sketch, "E82", {"start": v(133.72, 85.73) * mm, "end": v(72.49, 85.73) * mm});
            skLineSegment(sketch, "E83", {"start": v(72.49, 85.73) * mm, "end": v(18.28, 85.73) * mm});
            skLineSegment(sketch, "E84", {"start": v(18.28, 85.73) * mm, "end": v(22.4, 101.06) * mm});
            skLineSegment(sketch, "E85", {"start": v(22.4, 101.06) * mm, "end": v(45.16, 123.83) * mm});
            skLineSegment(sketch, "E86", {"start": v(45.16, 123.83) * mm, "end": v(57.86, 123.83) * mm});
            skLineSegment(sketch, "E87.0", {"start": v(47.13, 119.06) * mm, "end": v(57.86, 119.06) * mm});
            skLineSegment(sketch, "E87.1", {"start": v(26.66, 98.6) * mm, "end": v(47.13, 119.06) * mm});
            skLineSegment(sketch, "E87.2", {"start": v(22.88, 84.5) * mm, "end": v(26.66, 98.6) * mm});
            skLineSegment(sketch, "E88", {"start": v(57.86, 123.83) * mm, "end": v(57.86, 119.06) * mm});
            skSolve(sketch);
        }
        {
            var Q0;
            {var subQ1=sQuery(id+"F19.wireOp",EDGE,"E84");Q0=makeQuery(id+"F19.imprint","IMPRINT",FACE,{"disambiguationData":[TD([[makeQuery(id+"F19.imprint","IMPRINT",EDGE,{"derivedFrom":subQ1}),-1.0]])]});}
            var Q1;
            Q1=makeQuery(id+"F5.boolean.opBoolean","INTERSECT",EDGE,{"derivedFrom":[makeQuery(id+"F3.opExtrude","CAP_FACE",FACE,{"disambiguationData":[OSD([sQuery(id+"F2.wireOp",EDGE,"E1.0"),sQuery(id+"F2.wireOp",EDGE,"E1.1"),sQuery(id+"F2.wireOp",EDGE,"E1.2"),sQuery(id+"F2.wireOp",EDGE,"E1.3"),sQuery(id+"F2.wireOp",EDGE,"E1.4"),sQuery(id+"F2.wireOp",EDGE,"E1.5"),sQuery(id+"F2.wireOp",EDGE,"E1.6"),sQuery(id+"F2.wireOp",EDGE,"E1.7"),sQuery(id+"F2.wireOp",EDGE,"E1.8"),sQuery(id+"F2.wireOp",EDGE,"E1.9")])],"isStart":false}),makeQuery(id+"F5.opExtrude","SWEPT_FACE",FACE,{"disambiguationData":[OSD([sQuery(id+"F2.wireOp",EDGE,"E2.6")])]})]});
            var Q2;
            Q2=makeQuery(id+"F5.boolean.opBoolean","INTERSECT",EDGE,{"derivedFrom":[makeQuery(id+"F3.opExtrude","CAP_FACE",FACE,{"disambiguationData":[OSD([sQuery(id+"F2.wireOp",EDGE,"E1.0"),sQuery(id+"F2.wireOp",EDGE,"E1.1"),sQuery(id+"F2.wireOp",EDGE,"E1.2"),sQuery(id+"F2.wireOp",EDGE,"E1.3"),sQuery(id+"F2.wireOp",EDGE,"E1.4"),sQuery(id+"F2.wireOp",EDGE,"E1.5"),sQuery(id+"F2.wireOp",EDGE,"E1.6"),sQuery(id+"F2.wireOp",EDGE,"E1.7"),sQuery(id+"F2.wireOp",EDGE,"E1.8"),sQuery(id+"F2.wireOp",EDGE,"E1.9")])],"isStart":false}),makeQuery(id+"F5.opExtrude","SWEPT_FACE",FACE,{"disambiguationData":[OSD([sQuery(id+"F2.wireOp",EDGE,"E2.7")])]})]});
            var Q3;
            Q3=makeQuery(id+"F5.boolean.opBoolean","INTERSECT",EDGE,{"derivedFrom":[makeQuery(id+"F3.opExtrude","CAP_FACE",FACE,{"disambiguationData":[OSD([sQuery(id+"F2.wireOp",EDGE,"E1.0"),sQuery(id+"F2.wireOp",EDGE,"E1.1"),sQuery(id+"F2.wireOp",EDGE,"E1.2"),sQuery(id+"F2.wireOp",EDGE,"E1.3"),sQuery(id+"F2.wireOp",EDGE,"E1.4"),sQuery(id+"F2.wireOp",EDGE,"E1.5"),sQuery(id+"F2.wireOp",EDGE,"E1.6"),sQuery(id+"F2.wireOp",EDGE,"E1.7"),sQuery(id+"F2.wireOp",EDGE,"E1.8"),sQuery(id+"F2.wireOp",EDGE,"E1.9")])],"isStart":false}),makeQuery(id+"F5.opExtrude","SWEPT_FACE",FACE,{"disambiguationData":[OSD([sQuery(id+"F2.wireOp",EDGE,"E2.8")])]})]});
            var Q4;
            Q4=makeQuery(id+"F5.boolean.opBoolean","INTERSECT",EDGE,{"derivedFrom":[makeQuery(id+"F3.opExtrude","CAP_FACE",FACE,{"disambiguationData":[OSD([sQuery(id+"F2.wireOp",EDGE,"E1.0"),sQuery(id+"F2.wireOp",EDGE,"E1.1"),sQuery(id+"F2.wireOp",EDGE,"E1.2"),sQuery(id+"F2.wireOp",EDGE,"E1.3"),sQuery(id+"F2.wireOp",EDGE,"E1.4"),sQuery(id+"F2.wireOp",EDGE,"E1.5"),sQuery(id+"F2.wireOp",EDGE,"E1.6"),sQuery(id+"F2.wireOp",EDGE,"E1.7"),sQuery(id+"F2.wireOp",EDGE,"E1.8"),sQuery(id+"F2.wireOp",EDGE,"E1.9")])],"isStart":false}),makeQuery(id+"F5.opExtrude","SWEPT_FACE",FACE,{"disambiguationData":[OSD([sQuery(id+"F2.wireOp",EDGE,"E2.9")])]})]});
            var Q5;
            Q5=makeQuery(id+"F5.boolean.opBoolean","INTERSECT",EDGE,{"derivedFrom":[makeQuery(id+"F3.opExtrude","CAP_FACE",FACE,{"disambiguationData":[OSD([sQuery(id+"F2.wireOp",EDGE,"E1.0"),sQuery(id+"F2.wireOp",EDGE,"E1.1"),sQuery(id+"F2.wireOp",EDGE,"E1.2"),sQuery(id+"F2.wireOp",EDGE,"E1.3"),sQuery(id+"F2.wireOp",EDGE,"E1.4"),sQuery(id+"F2.wireOp",EDGE,"E1.5"),sQuery(id+"F2.wireOp",EDGE,"E1.6"),sQuery(id+"F2.wireOp",EDGE,"E1.7"),sQuery(id+"F2.wireOp",EDGE,"E1.8"),sQuery(id+"F2.wireOp",EDGE,"E1.9")])],"isStart":false}),makeQuery(id+"F5.opExtrude","SWEPT_FACE",FACE,{"disambiguationData":[OSD([sQuery(id+"F2.wireOp",EDGE,"E2.0")])]})]});
            var Q6;
            Q6=makeQuery(id+"F5.boolean.opBoolean","INTERSECT",EDGE,{"derivedFrom":[makeQuery(id+"F3.opExtrude","CAP_FACE",FACE,{"disambiguationData":[OSD([sQuery(id+"F2.wireOp",EDGE,"E1.0"),sQuery(id+"F2.wireOp",EDGE,"E1.1"),sQuery(id+"F2.wireOp",EDGE,"E1.2"),sQuery(id+"F2.wireOp",EDGE,"E1.3"),sQuery(id+"F2.wireOp",EDGE,"E1.4"),sQuery(id+"F2.wireOp",EDGE,"E1.5"),sQuery(id+"F2.wireOp",EDGE,"E1.6"),sQuery(id+"F2.wireOp",EDGE,"E1.7"),sQuery(id+"F2.wireOp",EDGE,"E1.8"),sQuery(id+"F2.wireOp",EDGE,"E1.9")])],"isStart":false}),makeQuery(id+"F5.opExtrude","SWEPT_FACE",FACE,{"disambiguationData":[OSD([sQuery(id+"F2.wireOp",EDGE,"E2.1")])]})]});
            var Q7;
            Q7=makeQuery(id+"F5.boolean.opBoolean","INTERSECT",EDGE,{"derivedFrom":[makeQuery(id+"F3.opExtrude","CAP_FACE",FACE,{"disambiguationData":[OSD([sQuery(id+"F2.wireOp",EDGE,"E1.0"),sQuery(id+"F2.wireOp",EDGE,"E1.1"),sQuery(id+"F2.wireOp",EDGE,"E1.2"),sQuery(id+"F2.wireOp",EDGE,"E1.3"),sQuery(id+"F2.wireOp",EDGE,"E1.4"),sQuery(id+"F2.wireOp",EDGE,"E1.5"),sQuery(id+"F2.wireOp",EDGE,"E1.6"),sQuery(id+"F2.wireOp",EDGE,"E1.7"),sQuery(id+"F2.wireOp",EDGE,"E1.8"),sQuery(id+"F2.wireOp",EDGE,"E1.9")])],"isStart":false}),makeQuery(id+"F5.opExtrude","SWEPT_FACE",FACE,{"disambiguationData":[OSD([sQuery(id+"F2.wireOp",EDGE,"E2.2")])]})]});
            var Q8;
            Q8=makeQuery(id+"F5.boolean.opBoolean","INTERSECT",EDGE,{"derivedFrom":[makeQuery(id+"F3.opExtrude","CAP_FACE",FACE,{"disambiguationData":[OSD([sQuery(id+"F2.wireOp",EDGE,"E1.0"),sQuery(id+"F2.wireOp",EDGE,"E1.1"),sQuery(id+"F2.wireOp",EDGE,"E1.2"),sQuery(id+"F2.wireOp",EDGE,"E1.3"),sQuery(id+"F2.wireOp",EDGE,"E1.4"),sQuery(id+"F2.wireOp",EDGE,"E1.5"),sQuery(id+"F2.wireOp",EDGE,"E1.6"),sQuery(id+"F2.wireOp",EDGE,"E1.7"),sQuery(id+"F2.wireOp",EDGE,"E1.8"),sQuery(id+"F2.wireOp",EDGE,"E1.9")])],"isStart":false}),makeQuery(id+"F5.opExtrude","SWEPT_FACE",FACE,{"disambiguationData":[OSD([sQuery(id+"F2.wireOp",EDGE,"E2.3")])]})]});
            var Q9;
            Q9=makeQuery(id+"F5.boolean.opBoolean","INTERSECT",EDGE,{"derivedFrom":[makeQuery(id+"F3.opExtrude","CAP_FACE",FACE,{"disambiguationData":[OSD([sQuery(id+"F2.wireOp",EDGE,"E1.0"),sQuery(id+"F2.wireOp",EDGE,"E1.1"),sQuery(id+"F2.wireOp",EDGE,"E1.2"),sQuery(id+"F2.wireOp",EDGE,"E1.3"),sQuery(id+"F2.wireOp",EDGE,"E1.4"),sQuery(id+"F2.wireOp",EDGE,"E1.5"),sQuery(id+"F2.wireOp",EDGE,"E1.6"),sQuery(id+"F2.wireOp",EDGE,"E1.7"),sQuery(id+"F2.wireOp",EDGE,"E1.8"),sQuery(id+"F2.wireOp",EDGE,"E1.9")])],"isStart":false}),makeQuery(id+"F5.opExtrude","SWEPT_FACE",FACE,{"disambiguationData":[OSD([sQuery(id+"F2.wireOp",EDGE,"E2.4")])]})]});
            var Q10;
            Q10=makeQuery(id+"F5.boolean.opBoolean","INTERSECT",EDGE,{"derivedFrom":[makeQuery(id+"F3.opExtrude","CAP_FACE",FACE,{"disambiguationData":[OSD([sQuery(id+"F2.wireOp",EDGE,"E1.0"),sQuery(id+"F2.wireOp",EDGE,"E1.1"),sQuery(id+"F2.wireOp",EDGE,"E1.2"),sQuery(id+"F2.wireOp",EDGE,"E1.3"),sQuery(id+"F2.wireOp",EDGE,"E1.4"),sQuery(id+"F2.wireOp",EDGE,"E1.5"),sQuery(id+"F2.wireOp",EDGE,"E1.6"),sQuery(id+"F2.wireOp",EDGE,"E1.7"),sQuery(id+"F2.wireOp",EDGE,"E1.8"),sQuery(id+"F2.wireOp",EDGE,"E1.9")])],"isStart":false}),makeQuery(id+"F5.opExtrude","SWEPT_FACE",FACE,{"disambiguationData":[OSD([sQuery(id+"F2.wireOp",EDGE,"E2.5")])]})]});
            sweep(context, id + "F20", {"operationType" : NewBodyOperationType.ADD, "profiles" : qUnion([Q0]), "path" : qUnion([Q1, Q2, Q3, Q4, Q5, Q6, Q7, Q8, Q9, Q10])});
        }
    });
